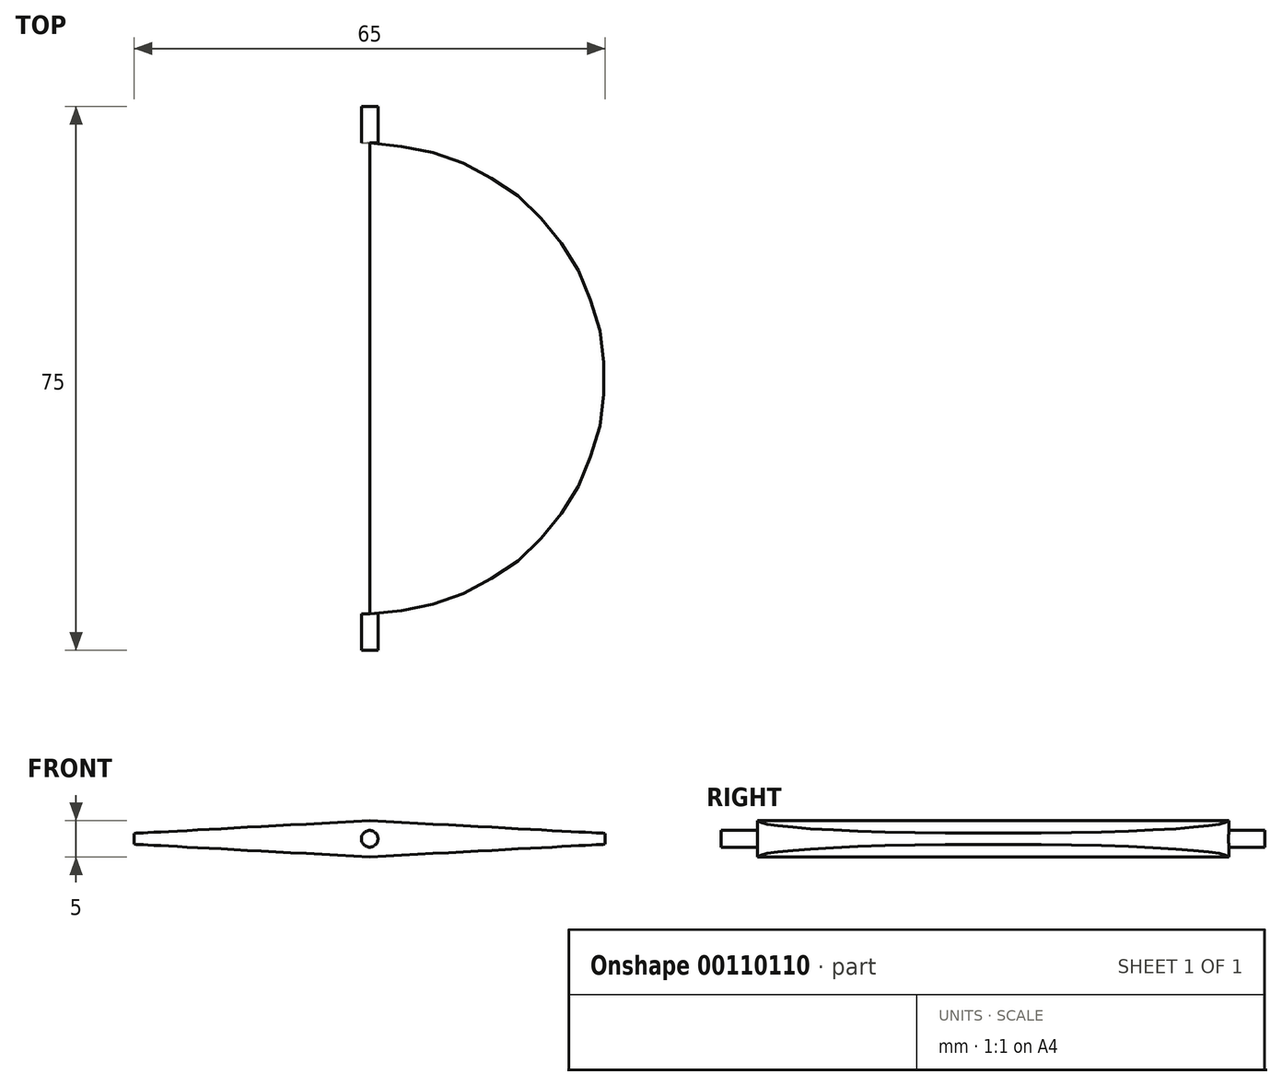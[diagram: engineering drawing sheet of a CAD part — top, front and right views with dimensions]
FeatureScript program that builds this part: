
annotation { "Feature Type Name" : "Feature", "Feature Type Description" : "" }
export const myFeature = defineFeature(function(context is Context, id is Id, definition is map)
    precondition{}
    {
        {
            var Q0;
            Q0=qCreatedBy(makeId("Front.planeOp"),FACE);
            var sketch = newSketch(context, id + "F0", { "sketchPlane" : qUnion([Q0])});
            skLineSegment(sketch, "E0", {"start": v(-32.5, 0.75) * mm, "end": v(-32.5, -0.75) * mm});
            skLineSegment(sketch, "E1", {"start": v(-32.5, -0.75) * mm, "end": v(0, -2.5) * mm});
            skLineSegment(sketch, "E2", {"start": v(32.5, -0.75) * mm, "end": v(32.5, 0.75) * mm});
            skLineSegment(sketch, "E3", {"start": v(0, 2.5) * mm, "end": v(-32.5, 0.75) * mm});
            skLineSegment(sketch, "E4", {"start": v(0, 2.5) * mm, "end": v(32.5, 0.75) * mm});
            skLineSegment(sketch, "E5", {"start": v(32.5, -0.75) * mm, "end": v(0, -2.5) * mm});
            skSolve(sketch);
        }
        {
            var Q0;
            Q0=makeQuery(id+"F0.imprint","IMPRINT",FACE,{"disambiguationData":[TD([[makeQuery(id+"F0.imprint","IMPRINT",EDGE,{"derivedFrom":sQuery(id+"F0.wireOp",EDGE,"E0")}),1.0]])]});
            extrude(context, id + "F1", {"entities" : qUnion([Q0]), "endBound" : BoundingType.SYMMETRIC, "depth" : 65 * mm});
        }
        {
            var Q0;
            Q0=qCreatedBy(makeId("Top.planeOp"),FACE);
            var sketch = newSketch(context, id + "F2", { "sketchPlane" : qUnion([Q0])});
            skCircle(sketch, "E6", {"center": v(0, 0) * mm, "radius": 32.5 * mm});
            skLineSegment(sketch, "E7.bottom", {"start": v(35, -35) * mm, "end": v(-35, -35) * mm});
            skLineSegment(sketch, "E7.top", {"start": v(35, 35) * mm, "end": v(-35, 35) * mm});
            skLineSegment(sketch, "E7.left", {"start": v(35, -35) * mm, "end": v(35, 35) * mm});
            skLineSegment(sketch, "E7.right", {"start": v(-35, -35) * mm, "end": v(-35, 35) * mm});
            skSolve(sketch);
        }
        {
            var Q0;
            Q0=makeQuery(id+"F2.imprint","IMPRINT",FACE,{"disambiguationData":[TD([[makeQuery(id+"F2.imprint","IMPRINT",EDGE,{"derivedFrom":sQuery(id+"F2.wireOp",EDGE,"E6")}),-1.0]])]});
            extrude(context, id + "F3", {"entities" : qUnion([Q0]), "endBound" : BoundingType.SYMMETRIC, "depth" : 10 * mm});
        }
        {
            var Q0;
            Q0=makeQuery(id+"F3.opExtrude","SWEPT_BODY",BODY,{"disambiguationData":[OSD([sQuery(id+"F2.wireOp",EDGE,"E6"),sQuery(id+"F2.wireOp",EDGE,"E7.bottom"),sQuery(id+"F2.wireOp",EDGE,"E7.top"),sQuery(id+"F2.wireOp",EDGE,"E7.left"),sQuery(id+"F2.wireOp",EDGE,"E7.right")])]});
            var Q1;
            Q1=makeQuery(id+"F1.opExtrude","SWEPT_BODY",BODY,{"disambiguationData":[OSD([sQuery(id+"F0.wireOp",EDGE,"E0"),sQuery(id+"F0.wireOp",EDGE,"E1"),sQuery(id+"F0.wireOp",EDGE,"E2"),sQuery(id+"F0.wireOp",EDGE,"E3"),sQuery(id+"F0.wireOp",EDGE,"E4"),sQuery(id+"F0.wireOp",EDGE,"E5")])]});
            booleanBodies(context, id + "F4", {"operationType" : BooleanOperationType.SUBTRACTION, "tools" : qUnion([Q0]), "targets" : qUnion([Q1])});
        }
        {
            var Q0;
            Q0=qCreatedBy(makeId("Front.planeOp"),FACE);
            var sketch = newSketch(context, id + "F5", { "sketchPlane" : qUnion([Q0])});
            skCircle(sketch, "E8", {"center": v(0, 0) * mm, "radius": 1.15 * mm});
            skSolve(sketch);
        }
        {
            var Q0;
            Q0=makeQuery(id+"F5.imprint","IMPRINT",FACE,{"disambiguationData":[TD([[makeQuery(id+"F5.imprint","IMPRINT",EDGE,{"derivedFrom":sQuery(id+"F5.wireOp",EDGE,"E8")}),1.0]])]});
            extrude(context, id + "F6", {"entities" : qUnion([Q0]), "operationType" : NewBodyOperationType.ADD, "endBound" : BoundingType.SYMMETRIC, "depth" : 75 * mm});
        }
    });
